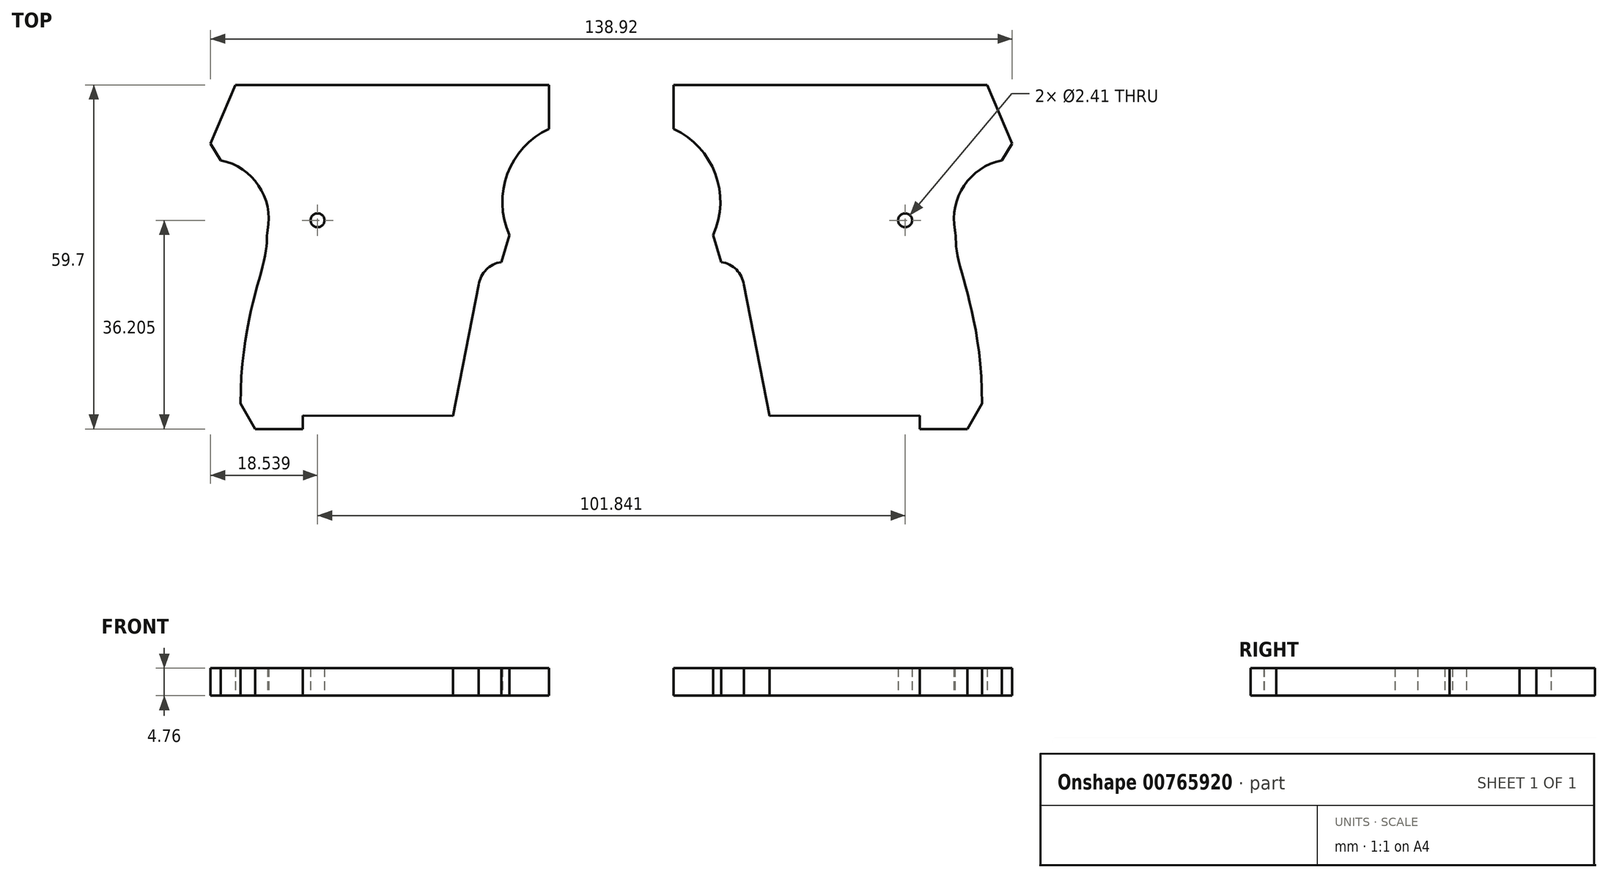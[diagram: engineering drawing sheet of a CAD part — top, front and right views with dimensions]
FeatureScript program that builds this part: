
annotation { "Feature Type Name" : "Feature", "Feature Type Description" : "" }
export const myFeature = defineFeature(function(context is Context, id is Id, definition is map)
    precondition{}
    {
        {
            var Q0;
            Q0=qCreatedBy(makeId("Top.planeOp"),FACE);
            var sketch = newSketch(context, id + "F0", { "sketchPlane" : qUnion([Q0])});
            skLineSegment(sketch, "E0", {"start": v(-69.46, 66.9) * mm, "end": v(-10.79, 66.9) * mm, "construction": true});
            skLineSegment(sketch, "E1", {"start": v(-69.46, 66.9) * mm, "end": v(-69.46, 7.22) * mm, "construction": true});
            skLineSegment(sketch, "E2", {"start": v(-66.94, 43.41) * mm, "end": v(-11.21, 43.41) * mm, "construction": true});
            skLineSegment(sketch, "E3", {"start": v(-50.92, 60.49) * mm, "end": v(-50.92, 7.21) * mm, "construction": true});
            skLineSegment(sketch, "E4", {"start": v(-26.95, 59.29) * mm, "end": v(-10.06, 59.29) * mm, "construction": true});
            skLineSegment(sketch, "E5", {"start": v(-71.7, 56.75) * mm, "end": v(-56.12, 56.75) * mm, "construction": true});
            skLineSegment(sketch, "E6", {"start": v(-28.57, 48.94) * mm, "end": v(-28.57, 36.23) * mm, "construction": true});
            skLineSegment(sketch, "E7", {"start": v(-10.79, 66.9) * mm, "end": v(-10.79, 9.5) * mm, "construction": true});
            skLineSegment(sketch, "E8", {"start": v(-64.26, 27) * mm, "end": v(-64.26, 7.22) * mm, "construction": true});
            skLineSegment(sketch, "E9", {"start": v(-27.43, 25.4) * mm, "end": v(-27.43, 9.5) * mm, "construction": true});
            skLineSegment(sketch, "E10", {"start": v(-17.65, 50.24) * mm, "end": v(-17.65, 39.7) * mm, "construction": true});
            skLineSegment(sketch, "E11", {"start": v(-53.46, 13.56) * mm, "end": v(-53.46, 7.21) * mm, "construction": true});
            skLineSegment(sketch, "E12", {"start": v(-65.14, 69) * mm, "end": v(-65.14, 61.5) * mm, "construction": true});
            skLineSegment(sketch, "E13", {"start": v(-59.56, 45.62) * mm, "end": v(-59.56, 36.09) * mm, "construction": true});
            skLineSegment(sketch, "E14", {"start": v(-71.28, 53.83) * mm, "end": v(-65.14, 53.83) * mm, "construction": true});
            skLineSegment(sketch, "E15", {"start": v(-67.68, 52.4) * mm, "end": v(-67.68, 46.92) * mm, "construction": true});
            skLineSegment(sketch, "E16", {"start": v(-65.14, 66.9) * mm, "end": v(-69.46, 56.75) * mm});
            skLineSegment(sketch, "E17", {"start": v(-69.46, 56.75) * mm, "end": v(-67.68, 53.83) * mm});
            skLineSegment(sketch, "E18", {"start": v(-59.56, 42.82) * mm, "end": v(-59.53, 42.82) * mm, "construction": true});
            skPoint(sketch, "E19", {"position": v(-59.56, 41.69) * mm});
            skArc(sketch, "E20", {"start": v(-59.56, 41.69) * mm, "mid": v(-61.13, 49.42) * mm, "end": v(-67.68, 53.83) * mm});
            skPoint(sketch, "E21", {"position": v(-59.9, 37.83) * mm});
            skLineSegment(sketch, "E22", {"start": v(-65.78, 11.66) * mm, "end": v(-61.78, 11.66) * mm, "construction": true});
            skFitSpline(sketch, "E23", {"points": [v(-59.56, 41.69) * mm, v(-59.9, 37.83) * mm, v(-64.26, 11.66) * mm], "startDerivative": vector(-2.23, -9.53) * mm, "endDerivative": vector(0, -56.66) * mm});
            skLineSegment(sketch, "E24", {"start": v(-61.72, 10.23) * mm, "end": v(-61.72, 5.63) * mm, "construction": true});
            skLineSegment(sketch, "E25", {"start": v(-64.26, 11.66) * mm, "end": v(-61.72, 7.22) * mm});
            skLineSegment(sketch, "E26", {"start": v(-61.72, 7.22) * mm, "end": v(-53.46, 7.21) * mm});
            skLineSegment(sketch, "E27", {"start": v(-27.43, 9.5) * mm, "end": v(-53.46, 9.53) * mm});
            skLineSegment(sketch, "E28", {"start": v(-53.46, 9.53) * mm, "end": v(-53.46, 7.21) * mm});
            skLineSegment(sketch, "E29", {"start": v(-65.14, 66.9) * mm, "end": v(-10.79, 66.9) * mm});
            skLineSegment(sketch, "E30", {"start": v(-10.79, 66.9) * mm, "end": v(-10.79, 59.29) * mm});
            skCircle(sketch, "E31", {"center": v(-50.92, 43.41) * mm, "radius": 1.2 * mm});
            skPoint(sketch, "E32", {"position": v(-17.65, 40.85) * mm});
            skArc(sketch, "E33", {"start": v(-10.79, 59.29) * mm, "mid": v(-18.01, 51.48) * mm, "end": v(-17.65, 40.85) * mm});
            skLineSegment(sketch, "E34", {"start": v(-20.38, 36.15) * mm, "end": v(-15.03, 36.15) * mm, "construction": true});
            skLineSegment(sketch, "E35", {"start": v(-19.04, 39.4) * mm, "end": v(-19.04, 32.6) * mm, "construction": true});
            skLineSegment(sketch, "E36", {"start": v(-17.65, 40.85) * mm, "end": v(-19.04, 36.15) * mm});
            skLineSegment(sketch, "E37", {"start": v(-22.98, 32.22) * mm, "end": v(-17.75, 32.22) * mm, "construction": true});
            skArc(sketch, "E38", {"start": v(-19.04, 36.15) * mm, "mid": v(-21.68, 34.85) * mm, "end": v(-22.98, 32.22) * mm});
            skLineSegment(sketch, "E39", {"start": v(-22.98, 32.22) * mm, "end": v(-27.43, 9.5) * mm});
            skLineSegment(sketch, "E40", {"start": v(0, 75.7) * mm, "end": v(0, 0) * mm, "construction": true});
            skLineSegment(sketch, "E41.MirrorCS", {"start": v(65.78, 11.66) * mm, "end": v(61.78, 11.66) * mm, "construction": true});
            skLineSegment(sketch, "E42.MirrorCS", {"start": v(59.56, 42.82) * mm, "end": v(59.53, 42.82) * mm, "construction": true});
            skLineSegment(sketch, "E43.MirrorCS", {"start": v(61.72, 10.23) * mm, "end": v(61.72, 5.63) * mm, "construction": true});
            skLineSegment(sketch, "E44.MirrorCS", {"start": v(64.26, 11.66) * mm, "end": v(61.72, 7.22) * mm});
            skLineSegment(sketch, "E45.MirrorCS", {"start": v(53.46, 9.53) * mm, "end": v(53.46, 7.21) * mm});
            skLineSegment(sketch, "E46.MirrorCS", {"start": v(69.46, 56.75) * mm, "end": v(67.68, 53.83) * mm});
            skLineSegment(sketch, "E47.MirrorCS", {"start": v(19.04, 39.4) * mm, "end": v(19.04, 32.6) * mm, "construction": true});
            skLineSegment(sketch, "E48.MirrorCS", {"start": v(17.65, 40.85) * mm, "end": v(19.04, 36.15) * mm});
            skArc(sketch, "E49.MirrorCS", {"start": v(19.04, 36.15) * mm, "mid": v(21.68, 34.85) * mm, "end": v(22.98, 32.22) * mm});
            skLineSegment(sketch, "E50.MirrorCS", {"start": v(59.56, 45.62) * mm, "end": v(59.56, 36.09) * mm, "construction": true});
            skLineSegment(sketch, "E51.MirrorCS", {"start": v(71.28, 53.83) * mm, "end": v(65.14, 53.83) * mm, "construction": true});
            skArc(sketch, "E52.MirrorCS", {"start": v(59.56, 41.69) * mm, "mid": v(61.13, 49.42) * mm, "end": v(67.68, 53.83) * mm});
            skLineSegment(sketch, "E53.MirrorCS", {"start": v(64.26, 27) * mm, "end": v(64.26, 7.22) * mm, "construction": true});
            skLineSegment(sketch, "E54.MirrorCS", {"start": v(20.38, 36.15) * mm, "end": v(15.03, 36.15) * mm, "construction": true});
            skLineSegment(sketch, "E55.MirrorCS", {"start": v(22.98, 32.22) * mm, "end": v(17.75, 32.22) * mm, "construction": true});
            skLineSegment(sketch, "E56.MirrorCS", {"start": v(17.65, 50.24) * mm, "end": v(17.65, 39.7) * mm, "construction": true});
            skLineSegment(sketch, "E57.MirrorCS", {"start": v(53.46, 13.56) * mm, "end": v(53.46, 7.21) * mm, "construction": true});
            skCircle(sketch, "E58.MirrorC", {"center": v(50.92, 43.41) * mm, "radius": 1.2 * mm});
            skLineSegment(sketch, "E59.MirrorCS", {"start": v(45.93, 33.77) * mm, "end": v(44.18, 32.4) * mm});
            skLineSegment(sketch, "E60.MirrorCS", {"start": v(65.14, 66.9) * mm, "end": v(69.46, 56.75) * mm});
            skLineSegment(sketch, "E61.MirrorCS", {"start": v(65.14, 69) * mm, "end": v(65.14, 61.5) * mm, "construction": true});
            skLineSegment(sketch, "E62.MirrorCS", {"start": v(67.68, 52.4) * mm, "end": v(67.68, 46.92) * mm, "construction": true});
            skLineSegment(sketch, "E63.MirrorCS", {"start": v(69.46, 66.9) * mm, "end": v(10.79, 66.9) * mm, "construction": true});
            skLineSegment(sketch, "E64.MirrorCS", {"start": v(61.72, 7.22) * mm, "end": v(53.46, 7.21) * mm});
            skLineSegment(sketch, "E65.MirrorCS", {"start": v(10.79, 66.9) * mm, "end": v(10.79, 9.5) * mm, "construction": true});
            skLineSegment(sketch, "E66.MirrorCS", {"start": v(28.57, 48.94) * mm, "end": v(28.57, 36.23) * mm, "construction": true});
            skLineSegment(sketch, "E67.MirrorCS", {"start": v(71.7, 56.75) * mm, "end": v(56.12, 56.75) * mm, "construction": true});
            skLineSegment(sketch, "E68.MirrorCS", {"start": v(66.94, 43.41) * mm, "end": v(11.21, 43.41) * mm, "construction": true});
            skLineSegment(sketch, "E69.MirrorCS", {"start": v(22.98, 32.22) * mm, "end": v(27.43, 9.5) * mm});
            skLineSegment(sketch, "E70.MirrorCS", {"start": v(65.14, 66.9) * mm, "end": v(10.79, 66.9) * mm});
            skPoint(sketch, "E71.MirrorP", {"position": v(17.65, 40.85) * mm});
            skPoint(sketch, "E72.MirrorP", {"position": v(59.9, 37.83) * mm});
            skFitSpline(sketch, "E73.MirrorCS", {"points": [v(59.56, 41.69) * mm, v(59.9, 37.83) * mm, v(64.26, 11.66) * mm], "startDerivative": vector(2.23, -9.53) * mm, "endDerivative": vector(0, -56.66) * mm});
            skArc(sketch, "E74.MirrorCS", {"start": v(10.79, 59.29) * mm, "mid": v(18.01, 51.48) * mm, "end": v(17.65, 40.85) * mm});
            skLineSegment(sketch, "E75.MirrorCS", {"start": v(27.43, 9.5) * mm, "end": v(53.46, 9.53) * mm});
            skLineSegment(sketch, "E76.MirrorCS", {"start": v(50.92, 60.49) * mm, "end": v(50.92, 7.21) * mm, "construction": true});
            skLineSegment(sketch, "E77.MirrorCS", {"start": v(10.79, 66.9) * mm, "end": v(10.79, 59.29) * mm});
            skLineSegment(sketch, "E78.MirrorCS", {"start": v(27.43, 25.4) * mm, "end": v(27.43, 9.5) * mm, "construction": true});
            skLineSegment(sketch, "E79.MirrorCS", {"start": v(69.46, 66.9) * mm, "end": v(69.46, 7.22) * mm, "construction": true});
            skLineSegment(sketch, "E80.MirrorCS", {"start": v(26.95, 59.29) * mm, "end": v(10.06, 59.29) * mm, "construction": true});
            skCircle(sketch, "E81", {"center": v(-28.57, 43.41) * mm, "radius": 2.37 * mm});
            skSolve(sketch);
        }
        {
            var Q0;
            Q0=makeQuery(id+"F0.imprint","IMPRINT",FACE,{"disambiguationData":[TD([[makeQuery(id+"F0.imprint","IMPRINT",EDGE,{"derivedFrom":sQuery(id+"F0.wireOp",EDGE,"E44.MirrorCS")}),-1.0]])]});
            var Q1;
            Q1=makeQuery(id+"F0.imprint","IMPRINT",FACE,{"disambiguationData":[TD([[makeQuery(id+"F0.imprint","IMPRINT",EDGE,{"derivedFrom":sQuery(id+"F0.wireOp",EDGE,"E16")}),1.0]])]});
            var Q2;
            Q2=makeQuery(id+"F0.imprint","IMPRINT",FACE,{"disambiguationData":[TD([[makeQuery(id+"F0.imprint","IMPRINT",EDGE,{"derivedFrom":sQuery(id+"F0.wireOp",EDGE,"E81")}),1.0]])]});
            extrude(context, id + "F1", {"entities" : qUnion([Q0, Q1, Q2]), "depth" : 4.76 * mm, "offsetDistance" : 25.4 * mm});
        }
    });
